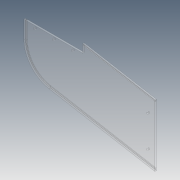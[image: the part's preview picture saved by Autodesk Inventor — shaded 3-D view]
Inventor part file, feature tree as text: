
AUTODESK INVENTOR PART (.ipt)
format: ipt  version: 2012 (Build 160160000, 160)  size: 130,560 bytes
history: native  units: in
note: dims shown in document units (in); Inventor stores cm internally (conversion verified against a paired STEP export)
features: extrude x3, sketch x2, hole x1, pattern_linear x1
ambient origin geometry x8: Origin, YZ Plane, XZ Plane, XY Plane, X Axis, Y Axis, Z Axis, Center Point
bodies: Solid1 (feature_tree)
feature tree (7):
  sketch  "Sketch1"  dims[d0=10.5in d2=0.0687in]
  extrude  "Extrusion1"  Depth=0.0687in
  extrude  "Extrusion2"  Depth=9.3125in
  extrude  "Extrusion3"  Depth=20.75in
  hole  "Hole1"  [1 undecoded]
  pattern_linear  "Rectangular Pattern1"  Spacing1=0.125in  [1 undecoded]
  sketch  "Sketch2"  dims[d3=9.625in d4=9.3125in d5=20.75in d6=0.25in d7=0.0in d14=0.125in d15=0.0in d18=4.813in d20=0.265in d21=2.375in d22=5.0in d23=1.1875in d24=1.1875in d25=1.0in d26=0.0in d27=0.1875in d28=0.125in d29=0.1875in d30=0.1875in d31=0.125in d32=0.125in d33=1.625in d34=0.5in d35=0.265in d36=0.75in d37=0.375in d38=0.25in d39=0.5635in d40=1.0in d41=0.8108in d42=1.1811in d44=3.0in]
note: 2 required parameter values undecoded (feature->parameter linkage not recoverable at this tier; creation-order binding heuristic only, values carry confidence <= 0.55)
